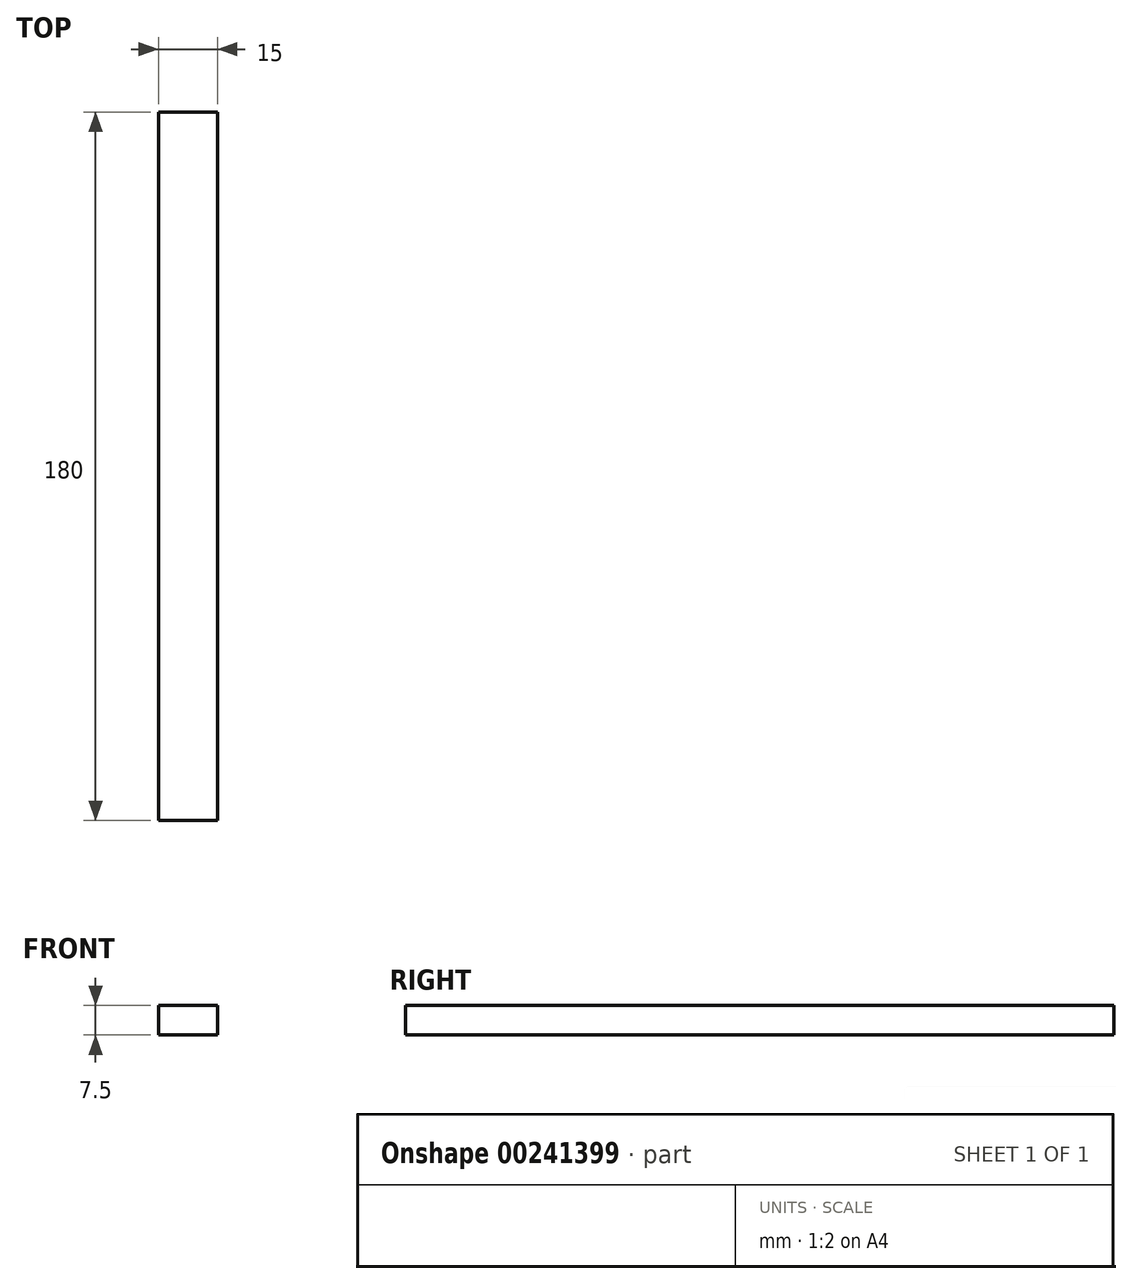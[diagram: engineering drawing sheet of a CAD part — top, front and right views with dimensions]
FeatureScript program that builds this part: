
annotation { "Feature Type Name" : "Feature", "Feature Type Description" : "" }
export const myFeature = defineFeature(function(context is Context, id is Id, definition is map)
    precondition{}
    {
        {
            var Q0;
            Q0=qCreatedBy(makeId("Front.planeOp"),FACE);
            var sketch = newSketch(context, id + "F0", { "sketchPlane" : qUnion([Q0])});
            skLineSegment(sketch, "E0.bottom", {"start": v(-7.5, 3.75) * mm, "end": v(7.5, 3.75) * mm});
            skLineSegment(sketch, "E0.top", {"start": v(-7.5, -3.75) * mm, "end": v(7.5, -3.75) * mm});
            skLineSegment(sketch, "E0.left", {"start": v(-7.5, 3.75) * mm, "end": v(-7.5, -3.75) * mm});
            skLineSegment(sketch, "E0.right", {"start": v(7.5, 3.75) * mm, "end": v(7.5, -3.75) * mm});
            skPoint(sketch, "E0.middle", {"position": v(0, 0) * mm});
            skSolve(sketch);
        }
        {
            var Q0;
            Q0 = qSketchRegion(id + "F0", true);
            extrude(context, id + "F1", {"entities" : qUnion([Q0]), "depth" : 180 * mm});
        }
    });
